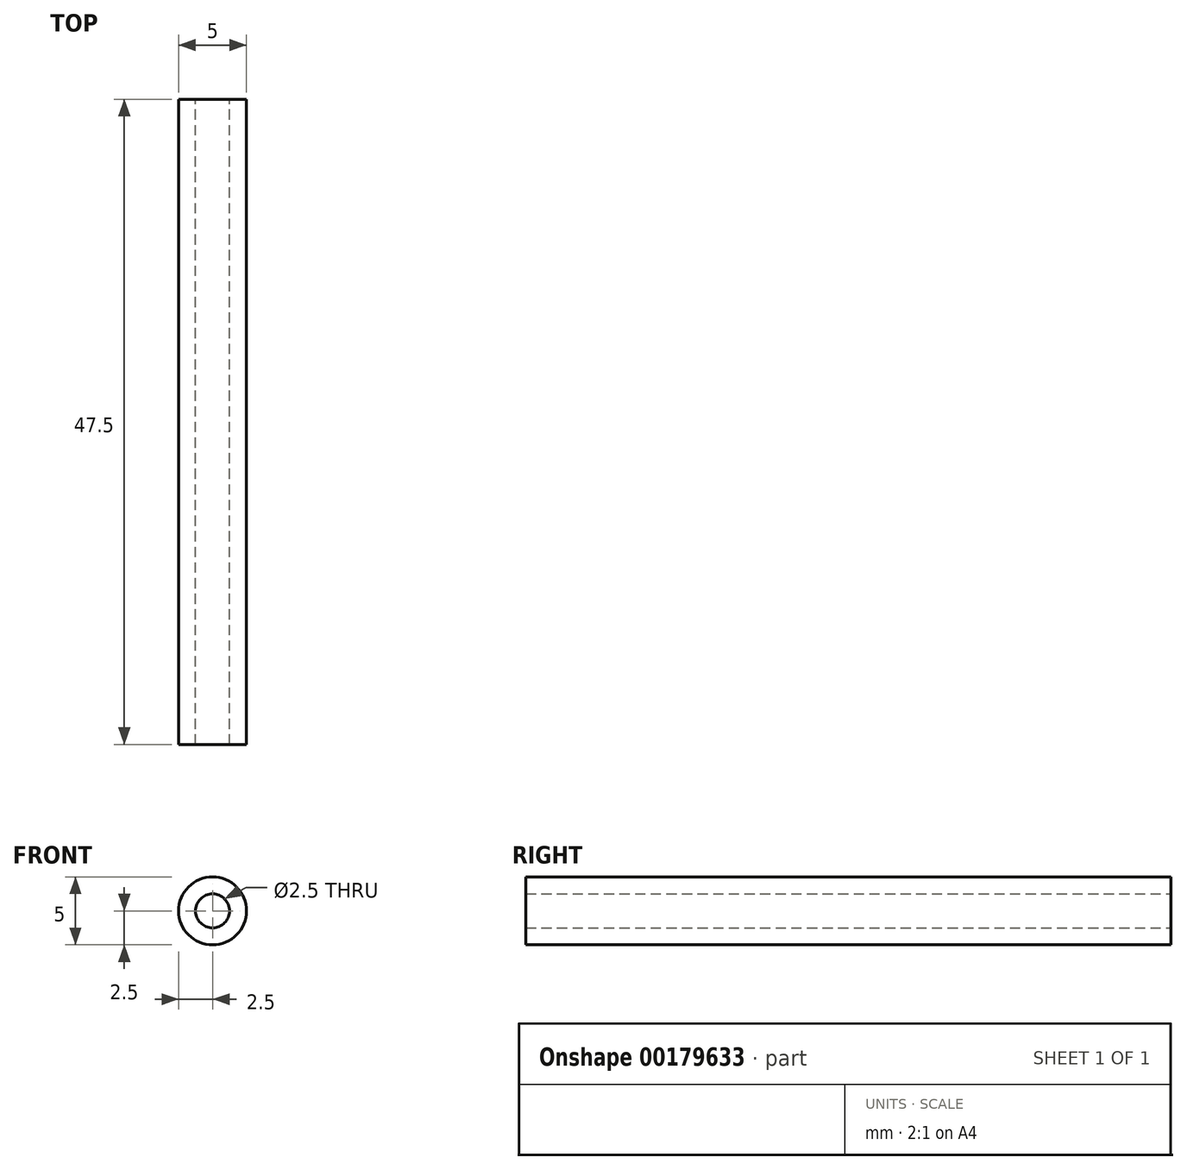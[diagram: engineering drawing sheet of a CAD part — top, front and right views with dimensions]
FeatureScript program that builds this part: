
annotation { "Feature Type Name" : "Feature", "Feature Type Description" : "" }
export const myFeature = defineFeature(function(context is Context, id is Id, definition is map)
    precondition{}
    {
        {
            var Q0;
            Q0=qCreatedBy(makeId("Top.planeOp"),FACE);
            var sketch = newSketch(context, id + "F0", { "sketchPlane" : qUnion([Q0])});
            skArc(sketch, "E0", {"start": v(16.57, -4.48) * mm, "mid": v(5.07, -9.38) * mm, "end": v(16.7, -13.95) * mm});
            skLineSegment(sketch, "E1.bottom", {"start": v(9.96, -5.28) * mm, "end": v(13.82, -5.28) * mm});
            skLineSegment(sketch, "E1.top", {"start": v(9.46, -13.28) * mm, "end": v(13.82, -13.28) * mm});
            skLineSegment(sketch, "E1.left", {"start": v(8.96, -6.28) * mm, "end": v(8.96, -12.78) * mm});
            skLineSegment(sketch, "E1.right", {"start": v(14.82, -6.28) * mm, "end": v(14.82, -12.28) * mm});
            skPoint(sketch, "E2", {"position": v(14.82, -7.78) * mm});
            skPoint(sketch, "E3", {"position": v(14.82, -10.78) * mm});
            skFitSpline(sketch, "E4", {"points": [v(14.82, -7.78) * mm, v(16.32, -7.78) * mm, v(16.57, -4.48) * mm], "startDerivative": vector(3.21, -6.32) * mm, "endDerivative": vector(0.04, 7.82) * mm});
            skFitSpline(sketch, "E5", {"points": [v(14.82, -10.78) * mm, v(16.32, -10.78) * mm, v(16.7, -13.95) * mm], "startDerivative": vector(3.18, 4.95) * mm, "endDerivative": vector(-0.25, -7.8) * mm});
            skPoint(sketch, "E6.visualSharp", {"position": v(8.96, -5.28) * mm});
            skArc(sketch, "E6.filletArc", {"start": v(9.96, -5.28) * mm, "mid": v(9.25, -5.58) * mm, "end": v(8.96, -6.28) * mm});
            skPoint(sketch, "E7.visualSharp", {"position": v(8.96, -13.28) * mm});
            skArc(sketch, "E7.filletArc", {"start": v(8.96, -12.78) * mm, "mid": v(9.1, -13.14) * mm, "end": v(9.46, -13.28) * mm});
            skPoint(sketch, "E8.visualSharp", {"position": v(14.82, -13.28) * mm});
            skArc(sketch, "E8.filletArc", {"start": v(13.82, -13.28) * mm, "mid": v(14.53, -13) * mm, "end": v(14.82, -12.28) * mm});
            skPoint(sketch, "E9.visualSharp", {"position": v(14.82, -5.28) * mm});
            skArc(sketch, "E9.filletArc", {"start": v(14.82, -6.28) * mm, "mid": v(14.53, -5.58) * mm, "end": v(13.82, -5.28) * mm});
            skSolve(sketch);
        }
        {
            var Q0;
            Q0=makeQuery(id+"F0.imprint","IMPRINT",FACE,{"disambiguationData":[TD([[makeQuery(id+"F0.imprint","IMPRINT",EDGE,{"derivedFrom":sQuery(id+"F0.wireOp",EDGE,"E0")}),1.0]])]});
            extrude(context, id + "F1", {"entities" : qUnion([Q0]), "depth" : 2 * mm});
        }
        {
            var Q0;
            Q0=makeQuery(id+"F1.opExtrude","CAP_FACE",FACE,{"disambiguationData":[OSD([sQuery(id+"F0.wireOp",EDGE,"E0"),sQuery(id+"F0.wireOp",EDGE,"E1.bottom"),sQuery(id+"F0.wireOp",EDGE,"E1.top"),sQuery(id+"F0.wireOp",EDGE,"E1.left"),sQuery(id+"F0.wireOp",EDGE,"E1.right"),sQuery(id+"F0.wireOp",EDGE,"E4"),sQuery(id+"F0.wireOp",EDGE,"E5")])],"isStart":false});
            var sketch = newSketch(context, id + "F2", { "sketchPlane" : qUnion([Q0])});
            skArc(sketch, "E10", {"start": v(15.84, -2.65) * mm, "mid": v(12.03, -1.54) * mm, "end": v(8.17, -2.45) * mm});
            skFitSpline(sketch, "E11", {"points": [v(15.87, -15.9) * mm, v(16.7, -13.95) * mm], "startDerivative": vector(2.83, 2.73) * mm, "endDerivative": vector(0.3, 2.18) * mm});
            skFitSpline(sketch, "E12", {"points": [v(7.38, -15.63) * mm, v(5.35, -16.17) * mm, v(4.09, -17.75) * mm], "startDerivative": vector(-6.5, -0.58) * mm, "endDerivative": vector(-7.65, -9.56) * mm});
            skPoint(sketch, "E13.startSnap0", {"position": v(4.07, -9.3) * mm});
            skFitSpline(sketch, "E14", {"points": [v(8.17, -2.45) * mm, v(5.9, -1.15) * mm, v(4.09, 1.29) * mm], "startDerivative": vector(-4.7, 3.1) * mm, "endDerivative": vector(-2.62, 5.24) * mm});
            skLineSegment(sketch, "E15", {"start": v(4.09, 1.29) * mm, "end": v(4.09, -17.75) * mm});
            skArc(sketch, "E16.trimOffspring", {"start": v(4.09, -8.77) * mm, "mid": v(4.08, -9.04) * mm, "end": v(4.07, -9.3) * mm});
            skArc(sketch, "E17.trimOffspring", {"start": v(7.38, -15.63) * mm, "mid": v(11.59, -17.03) * mm, "end": v(15.87, -15.9) * mm});
            skArc(sketch, "E18", {"start": v(16.6, -5.66) * mm, "mid": v(5.82, -9.4) * mm, "end": v(16.74, -12.72) * mm});
            skFitSpline(sketch, "E19", {"points": [v(15.84, -2.65) * mm, v(16.57, -4.48) * mm], "startDerivative": vector(0.73, -1.83) * mm, "endDerivative": vector(0.73, -1.83) * mm});
            skFitSpline(sketch, "E20", {"points": [v(16.57, -4.48) * mm, v(16.6, -5.66) * mm], "startDerivative": vector(0.04, -1.18) * mm, "endDerivative": vector(0.04, -1.18) * mm});
            skFitSpline(sketch, "E21", {"points": [v(16.7, -13.95) * mm, v(16.74, -12.72) * mm], "startDerivative": vector(0.04, 1.23) * mm, "endDerivative": vector(0.04, 1.23) * mm});
            skSolve(sketch);
        }
        {
            var Q0;
            Q0=makeQuery(id+"F2.imprint","IMPRINT",FACE,{"disambiguationData":[TD([[makeQuery(id+"F2.imprint","IMPRINT",EDGE,{"derivedFrom":sQuery(id+"F2.wireOp",EDGE,"E10")}),1.0]])]});
            var Q1;
            {var subQ1=sQuery(id+"F2.wireOp",EDGE,"E18");Q1=makeQuery(id+"F2.imprint","IMPRINT",FACE,{"disambiguationData":[TD([[makeQuery(id+"F2.imprint","IMPRINT",EDGE,{"derivedFrom":subQ1}),-1.0]])]});}
            extrude(context, id + "F3", {"entities" : qUnion([Q0, Q1]), "operationType" : NewBodyOperationType.ADD, "depth" : .5 * mm, "hasSecondDirection" : true, "secondDirectionOppositeDirection" : true, "secondDirectionDepth" : 2.5 * mm});
        }
        {
            var Q0;
            Q0=qCreatedBy(makeId("Front.planeOp"),FACE);
            var sketch = newSketch(context, id + "F4", { "sketchPlane" : qUnion([Q0])});
            skCircle(sketch, "E22", {"center": v(4.09, 1) * mm, "radius": 1.25 * mm});
            skCircle(sketch, "E23", {"center": v(4.09, 1) * mm, "radius": 2.5 * mm});
            skSolve(sketch);
        }
        {
            var Q0;
            Q0=makeQuery(id+"F4.imprint","IMPRINT",FACE,{"disambiguationData":[TD([[makeQuery(id+"F4.imprint","IMPRINT",EDGE,{"derivedFrom":sQuery(id+"F4.wireOp",EDGE,"E22")}),-1.0]])]});
            extrude(context, id + "F5", {"entities" : qUnion([Q0]), "depth" : 46 * mm, "hasSecondDirection" : true, "secondDirectionOppositeDirection" : true, "secondDirectionDepth" : 1.5 * mm});
        }
        {
            var Q0;
            Q0=makeQuery(id+"F5.opExtrude","SWEPT_BODY",BODY,{"disambiguationData":[OSD([sQuery(id+"F4.wireOp",EDGE,"E22"),sQuery(id+"F4.wireOp",EDGE,"E23")])]});
            var Q1;
            Q1=makeQuery(id+"F1.opExtrude","SWEPT_BODY",BODY,{"disambiguationData":[OSD([sQuery(id+"F0.wireOp",EDGE,"E0"),sQuery(id+"F0.wireOp",EDGE,"E1.bottom"),sQuery(id+"F0.wireOp",EDGE,"E1.top"),sQuery(id+"F0.wireOp",EDGE,"E1.left"),sQuery(id+"F0.wireOp",EDGE,"E1.right"),sQuery(id+"F0.wireOp",EDGE,"E4"),sQuery(id+"F0.wireOp",EDGE,"E5")])]});
            booleanBodies(context, id + "F6", {"operationType" : BooleanOperationType.SUBTRACTION, "tools" : qUnion([Q0]), "targets" : qUnion([Q1]), "keepTools" : true});
        }
        {
            var Q0;
            Q0=makeQuery(id+"F6.opBoolean","SPLIT",BODY,{"disambiguationData":[OD(0.0)],"derivedFrom":makeQuery(id+"F1.opExtrude","SWEPT_BODY",BODY,{"disambiguationData":[OSD([sQuery(id+"F0.wireOp",EDGE,"E0"),sQuery(id+"F0.wireOp",EDGE,"E1.bottom"),sQuery(id+"F0.wireOp",EDGE,"E1.top"),sQuery(id+"F0.wireOp",EDGE,"E1.left"),sQuery(id+"F0.wireOp",EDGE,"E1.right"),sQuery(id+"F0.wireOp",EDGE,"E4"),sQuery(id+"F0.wireOp",EDGE,"E5")])]})});
            deleteBodies(context, id + "F7", {"entities" : qUnion([Q0])});
        }
    });
